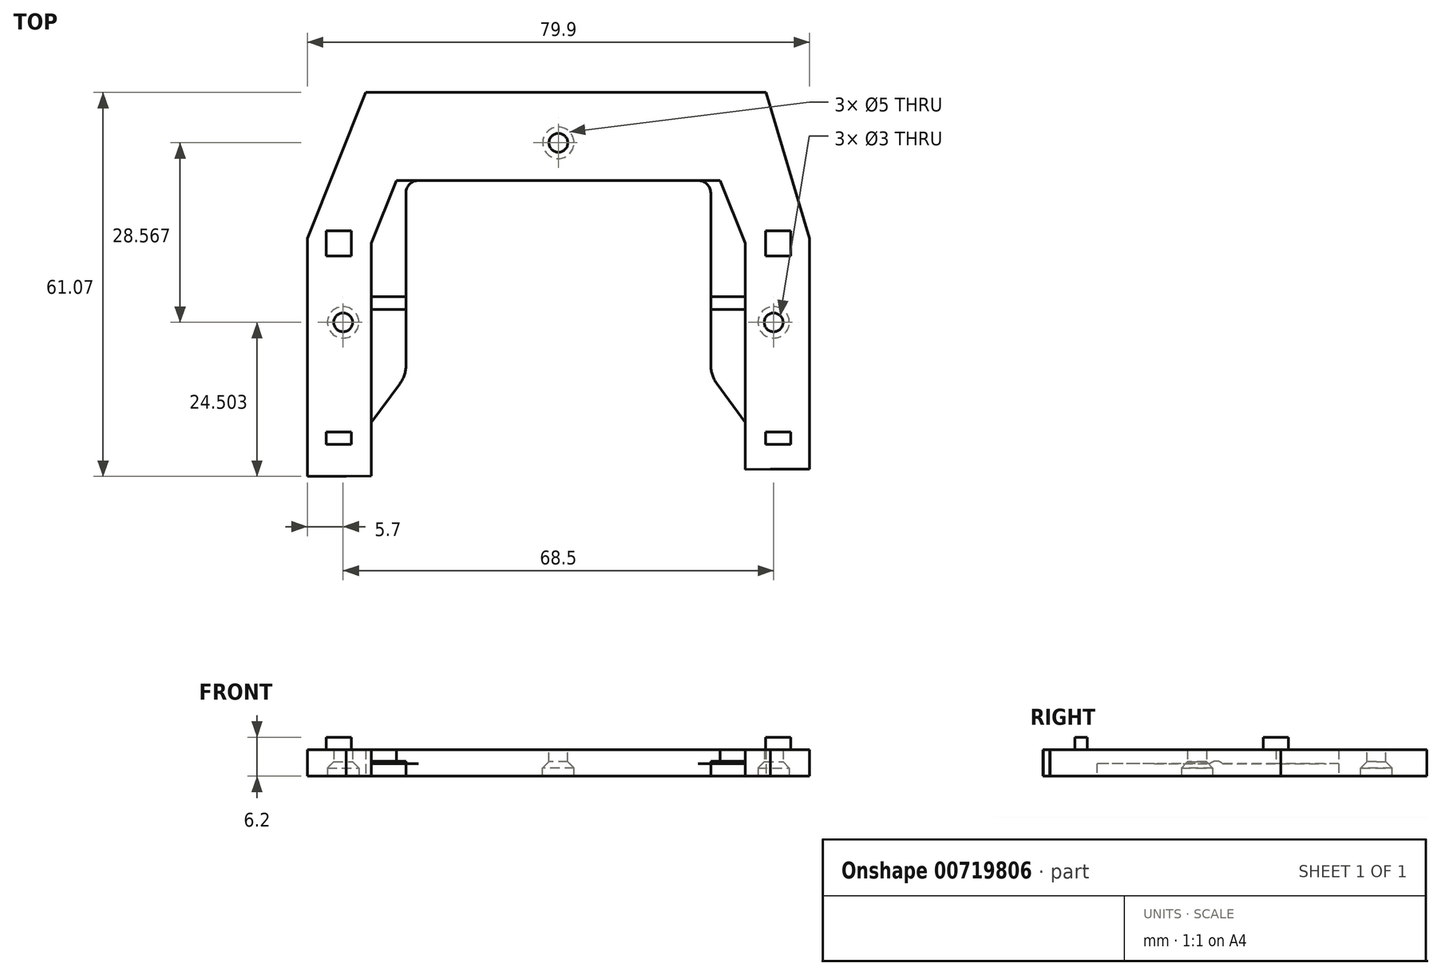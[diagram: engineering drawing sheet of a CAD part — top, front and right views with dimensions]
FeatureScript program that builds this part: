
annotation { "Feature Type Name" : "Feature", "Feature Type Description" : "" }
export const myFeature = defineFeature(function(context is Context, id is Id, definition is map)
    precondition{}
    {
        {
            var Q0;
            Q0=qCreatedBy(makeId("Top.planeOp"),FACE);
            var sketch = newSketch(context, id + "F0", { "sketchPlane" : qUnion([Q0])});
            skLineSegment(sketch, "E0.bottom", {"start": v(-25.5, 14.25) * mm, "end": v(26, 14.25) * mm});
            skLineSegment(sketch, "E0.left", {"start": v(-29.5, 4.25) * mm, "end": v(-29.5, -35.75) * mm});
            skLineSegment(sketch, "E0.right", {"start": v(30, 4.25) * mm, "end": v(30, -35.75) * mm});
            skLineSegment(sketch, "E1", {"start": v(-25.5, 14.25) * mm, "end": v(-29.5, 4.25) * mm});
            skPoint(sketch, "E2.orphan", {"position": v(-29.5, 14.25) * mm});
            skLineSegment(sketch, "E3", {"start": v(26, 14.25) * mm, "end": v(30, 4.25) * mm});
            skPoint(sketch, "E4.orphan", {"position": v(30, 14.25) * mm});
            skLineSegment(sketch, "E5.0", {"start": v(-24.2, 28.25) * mm, "end": v(-33.5, 5.02) * mm});
            skLineSegment(sketch, "E5.1", {"start": v(-33.5, -32.82) * mm, "end": v(34, -31.68) * mm});
            skLineSegment(sketch, "E5.2", {"start": v(34, 5.02) * mm, "end": v(34, -31.68) * mm});
            skLineSegment(sketch, "E5.3", {"start": v(-33.5, 5.02) * mm, "end": v(-33.5, -32.82) * mm});
            skLineSegment(sketch, "E5.4", {"start": v(27.1, 28.25) * mm, "end": v(34, 5.02) * mm});
            skLineSegment(sketch, "E5.5", {"start": v(-24.2, 28.25) * mm, "end": v(27.1, 28.25) * mm});
            skLineSegment(sketch, "E6", {"start": v(-29.5, -32.75) * mm, "end": v(-29.5, -35.75) * mm});
            skLineSegment(sketch, "E7", {"start": v(30, -32.75) * mm, "end": v(30, -35.75) * mm});
            skLineSegment(sketch, "E8.bottom", {"start": v(-29.5, -32.75) * mm, "end": v(30, -31.75) * mm});
            skLineSegment(sketch, "E8.left", {"start": v(-29.5, -32.75) * mm, "end": v(-29.5, -24.25) * mm});
            skLineSegment(sketch, "E8.right", {"start": v(30, -31.75) * mm, "end": v(30, -24.25) * mm});
            skLineSegment(sketch, "E9.top", {"start": v(-22, 14.25) * mm, "end": v(22.5, 14.25) * mm});
            skLineSegment(sketch, "E9.left", {"start": v(-24, -16.75) * mm, "end": v(-24, 12.25) * mm});
            skLineSegment(sketch, "E9.right", {"start": v(24.5, -16.75) * mm, "end": v(24.5, 12.25) * mm});
            skPoint(sketch, "E10.visualSharp", {"position": v(-24, 14.25) * mm});
            skArc(sketch, "E10.filletArc", {"start": v(-22, 14.25) * mm, "mid": v(-23.41, 13.66) * mm, "end": v(-24, 12.25) * mm});
            skPoint(sketch, "E11.visualSharp", {"position": v(24.5, 14.25) * mm});
            skArc(sketch, "E11.filletArc", {"start": v(24.5, 12.25) * mm, "mid": v(23.91, 13.66) * mm, "end": v(22.5, 14.25) * mm});
            skLineSegment(sketch, "E12", {"start": v(24.5, -16.75) * mm, "end": v(30, -24.25) * mm});
            skLineSegment(sketch, "E13", {"start": v(-24, -16.75) * mm, "end": v(-29.5, -24.25) * mm});
            skPoint(sketch, "E14.orphan", {"position": v(-29.5, -15.75) * mm});
            skPoint(sketch, "E15.orphan", {"position": v(30, -16.75) * mm});
            skSolve(sketch);
        }
        {
            var Q0;
            Q0=makeQuery(id+"F0.imprint","IMPRINT",FACE,{"disambiguationData":[TD([[makeQuery(id+"F0.imprint","IMPRINT",EDGE,{"derivedFrom":sQuery(id+"F0.wireOp",EDGE,"E0.bottom")}),-1.0]])]});
            extrude(context, id + "F1", {"entities" : qUnion([Q0]), "depth" : 2 * mm, "offsetDistance" : 25 * mm});
        }
        {
            var Q0;
            Q0=makeQuery(id+"F0.imprint","IMPRINT",FACE,{"disambiguationData":[TD([[makeQuery(id+"F0.imprint","IMPRINT",EDGE,{"derivedFrom":sQuery(id+"F0.wireOp",EDGE,"E0.bottom")}),1.0]])]});
            extrude(context, id + "F2", {"entities" : qUnion([Q0]), "operationType" : NewBodyOperationType.ADD, "depth" : 4.2 * mm, "offsetDistance" : 25 * mm});
        }
        {
            var Q0;
            Q0=makeQuery(id+"F2.opExtrude","SWEPT_FACE",FACE,{"disambiguationData":[OSD([sQuery(id+"F0.wireOp",EDGE,"E5.3")])]});
            var Q1;
            Q1=makeQuery(id+"F2.opExtrude","SWEPT_FACE",FACE,{"disambiguationData":[OSD([sQuery(id+"F0.wireOp",EDGE,"E5.0")])]});
            extrude(context, id + "F3", {"entities" : qUnion([Q0, Q1]), "operationType" : NewBodyOperationType.ADD, "depth" : 6.2 * mm, "offsetDistance" : 25 * mm});
        }
        {
            var Q0;
            Q0=makeQuery(id+"F2.opExtrude","SWEPT_FACE",FACE,{"disambiguationData":[OSD([sQuery(id+"F0.wireOp",EDGE,"E5.2")])]});
            var Q1;
            Q1=makeQuery(id+"F2.opExtrude","SWEPT_FACE",FACE,{"disambiguationData":[OSD([sQuery(id+"F0.wireOp",EDGE,"E5.4")])]});
            extrude(context, id + "F4", {"entities" : qUnion([Q0, Q1]), "operationType" : NewBodyOperationType.ADD, "depth" : 6.2 * mm, "offsetDistance" : 25 * mm});
        }
        {
            var Q0;
            {var subQ0=sQuery(id+"F0.wireOp",EDGE,"E5.4");var subQ1=sQuery(id+"F0.wireOp",EDGE,"E5.2");var subQ2=sQuery(id+"F0.wireOp",EDGE,"E5.3");var subQ3=sQuery(id+"F0.wireOp",EDGE,"E5.0");Q0=makeQuery(id+"F4.boolean.opBoolean","MERGE",FACE,{"derivedFrom":[makeQuery(id+"F3.boolean.opBoolean","MERGE",FACE,{"derivedFrom":[makeQuery(id+"F2.opExtrude","CAP_FACE",FACE,{"disambiguationData":[OSD([sQuery(id+"F0.wireOp",EDGE,"E0.bottom"),sQuery(id+"F0.wireOp",EDGE,"E0.left"),sQuery(id+"F0.wireOp",EDGE,"E0.right"),sQuery(id+"F0.wireOp",EDGE,"E1"),sQuery(id+"F0.wireOp",EDGE,"E3"),subQ3,sQuery(id+"F0.wireOp",EDGE,"E5.1"),subQ1,subQ2,subQ0,sQuery(id+"F0.wireOp",EDGE,"E5.5"),sQuery(id+"F0.wireOp",EDGE,"E8.left"),sQuery(id+"F0.wireOp",EDGE,"E8.right"),sQuery(id+"F0.wireOp",EDGE,"E9.top")])],"isStart":false}),makeQuery(id+"F3.opExtrude","SWEPT_FACE",FACE,{"disambiguationData":[OSD([subQ3]),TDD([makeQuery(id+"F2.opExtrude","CAP_EDGE",EDGE,{"disambiguationData":[OSD([subQ3])],"isStart":false})])]}),makeQuery(id+"F3.opExtrude","SWEPT_FACE",FACE,{"disambiguationData":[OSD([subQ2]),TDD([makeQuery(id+"F2.opExtrude","CAP_EDGE",EDGE,{"disambiguationData":[OSD([subQ2])],"isStart":false})])]})]}),makeQuery(id+"F4.opExtrude","SWEPT_FACE",FACE,{"disambiguationData":[OSD([subQ1]),TDD([makeQuery(id+"F2.opExtrude","CAP_EDGE",EDGE,{"disambiguationData":[OSD([subQ1])],"isStart":false})])]}),makeQuery(id+"F4.opExtrude","SWEPT_FACE",FACE,{"disambiguationData":[OSD([subQ0]),TDD([makeQuery(id+"F2.opExtrude","CAP_EDGE",EDGE,{"disambiguationData":[OSD([subQ0])],"isStart":false})])]})]});}
            var sketch = newSketch(context, id + "F5", { "sketchPlane" : qUnion([Q0])});
            skLineSegment(sketch, "E16.bottom", {"start": v(-36.7, -27.75) * mm, "end": v(-32.7, -27.75) * mm});
            skLineSegment(sketch, "E16.top", {"start": v(-36.7, -25.75) * mm, "end": v(-32.7, -25.75) * mm});
            skLineSegment(sketch, "E16.left", {"start": v(-36.7, -27.75) * mm, "end": v(-36.7, -25.75) * mm});
            skLineSegment(sketch, "E16.right", {"start": v(-32.7, -27.75) * mm, "end": v(-32.7, -25.75) * mm});
            skLineSegment(sketch, "E17.bottom", {"start": v(37.2, -27.75) * mm, "end": v(33.2, -27.75) * mm});
            skLineSegment(sketch, "E17.top", {"start": v(37.2, -25.75) * mm, "end": v(33.2, -25.75) * mm});
            skLineSegment(sketch, "E17.left", {"start": v(37.2, -27.75) * mm, "end": v(37.2, -25.75) * mm});
            skLineSegment(sketch, "E17.right", {"start": v(33.2, -27.75) * mm, "end": v(33.2, -25.75) * mm});
            skLineSegment(sketch, "E18.bottom", {"start": v(33.2, 2.25) * mm, "end": v(37.2, 2.25) * mm});
            skLineSegment(sketch, "E18.top", {"start": v(33.2, 6.25) * mm, "end": v(37.2, 6.25) * mm});
            skLineSegment(sketch, "E18.left", {"start": v(33.2, 2.25) * mm, "end": v(33.2, 6.25) * mm});
            skLineSegment(sketch, "E18.right", {"start": v(37.2, 2.25) * mm, "end": v(37.2, 6.25) * mm});
            skLineSegment(sketch, "E19.bottom", {"start": v(-36.7, 2.25) * mm, "end": v(-32.7, 2.25) * mm});
            skLineSegment(sketch, "E19.top", {"start": v(-36.7, 6.25) * mm, "end": v(-32.7, 6.25) * mm});
            skLineSegment(sketch, "E19.left", {"start": v(-36.7, 2.25) * mm, "end": v(-36.7, 6.25) * mm});
            skLineSegment(sketch, "E19.right", {"start": v(-32.7, 2.25) * mm, "end": v(-32.7, 6.25) * mm});
            skSolve(sketch);
        }
        {
            var Q0;
            Q0=qSketchRegion(id+"F5",true);
            extrude(context, id + "F6", {"entities" : qUnion([Q0]), "operationType" : NewBodyOperationType.ADD, "depth" : 2 * mm, "offsetDistance" : 25 * mm});
        }
        {
            var Q0;
            {var subQ0=sQuery(id+"F0.wireOp",EDGE,"E5.3");var subQ1=sQuery(id+"F0.wireOp",EDGE,"E5.0");var subQ2=sQuery(id+"F0.wireOp",EDGE,"E3");var subQ3=sQuery(id+"F0.wireOp",EDGE,"E1");var subQ4=sQuery(id+"F0.wireOp",EDGE,"E0.right");var subQ5=sQuery(id+"F0.wireOp",EDGE,"E0.left");var subQ6=sQuery(id+"F0.wireOp",EDGE,"E0.bottom");Q0=makeQuery(id+"F3.boolean.opBoolean","MERGE",FACE,{"derivedFrom":[makeQuery(id+"FPUi8WWa0XVN5Qz_1.opFillet","SPLIT",FACE,{"disambiguationData":[OD(0.0)],"derivedFrom":makeQuery(id+"F2.boolean.opBoolean","MERGE",FACE,{"derivedFrom":[makeQuery(id+"F1.opExtrude","CAP_FACE",FACE,{"disambiguationData":[OSD([subQ6,subQ5,subQ3,sQuery(id+"F0.wireOp",EDGE,"E9.left"),sQuery(id+"F0.wireOp",EDGE,"E10.filletArc"),sQuery(id+"F0.wireOp",EDGE,"E13")])],"isStart":true}),makeQuery(id+"F1.opExtrude","CAP_FACE",FACE,{"disambiguationData":[OSD([subQ6,subQ4,subQ2,sQuery(id+"F0.wireOp",EDGE,"E9.right"),sQuery(id+"F0.wireOp",EDGE,"E11.filletArc"),sQuery(id+"F0.wireOp",EDGE,"E12")])],"isStart":true}),makeQuery(id+"F2.opExtrude","CAP_FACE",FACE,{"disambiguationData":[OSD([subQ6,subQ5,subQ4,subQ3,subQ2,subQ1,sQuery(id+"F0.wireOp",EDGE,"E5.1"),sQuery(id+"F0.wireOp",EDGE,"E5.2"),subQ0,sQuery(id+"F0.wireOp",EDGE,"E5.4"),sQuery(id+"F0.wireOp",EDGE,"E5.5"),sQuery(id+"F0.wireOp",EDGE,"E8.left"),sQuery(id+"F0.wireOp",EDGE,"E8.right"),sQuery(id+"F0.wireOp",EDGE,"E9.top")])],"isStart":true})]})}),makeQuery(id+"F3.opExtrude","SWEPT_FACE",FACE,{"disambiguationData":[OSD([subQ1]),TDD([makeQuery(id+"F2.opExtrude","CAP_EDGE",EDGE,{"disambiguationData":[OSD([subQ1])],"isStart":true})])]}),makeQuery(id+"F3.opExtrude","SWEPT_FACE",FACE,{"disambiguationData":[OSD([subQ0]),TDD([makeQuery(id+"F2.opExtrude","CAP_EDGE",EDGE,{"disambiguationData":[OSD([subQ0])],"isStart":true})])]})]});}
            var sketch = newSketch(context, id + "F7", { "sketchPlane" : qUnion([Q0])});
            skCircle(sketch, "E20", {"center": v(-34, 8.32) * mm, "radius": 2.5 * mm});
            skCircle(sketch, "E21", {"center": v(34.5, 8.32) * mm, "radius": 2.5 * mm});
            skCircle(sketch, "E22", {"center": v(-34, 8.32) * mm, "radius": 1.5 * mm});
            skCircle(sketch, "E23", {"center": v(34.5, 8.32) * mm, "radius": 1.5 * mm});
            skSolve(sketch);
        }
        {
            var Q0;
            Q0=qSketchRegion(id+"F7",true);
            extrude(context, id + "F8", {"entities" : qUnion([Q0]), "operationType" : NewBodyOperationType.REMOVE, "oppositeDirection" : true, "depth" : 2.5 * mm, "offsetDistance" : 25 * mm});
        }
        {
            var Q0;
            {var subQ0=sQuery(id+"F0.wireOp",EDGE,"E5.3");var subQ1=sQuery(id+"F0.wireOp",EDGE,"E5.0");var subQ2=sQuery(id+"F0.wireOp",EDGE,"E3");var subQ3=sQuery(id+"F0.wireOp",EDGE,"E1");var subQ4=sQuery(id+"F0.wireOp",EDGE,"E0.right");var subQ5=sQuery(id+"F0.wireOp",EDGE,"E0.left");var subQ6=sQuery(id+"F0.wireOp",EDGE,"E0.bottom");Q0=makeQuery(id+"F8.boolean.opBoolean","SPLIT",FACE,{"disambiguationData":[TD([makeQuery(id+"F8.opExtrude","SWEPT_FACE",FACE,{"disambiguationData":[OSD([sQuery(id+"F7.wireOp",EDGE,"E22")])]})])],"derivedFrom":makeQuery(id+"F3.boolean.opBoolean","MERGE",FACE,{"derivedFrom":[makeQuery(id+"FPUi8WWa0XVN5Qz_1.opFillet","SPLIT",FACE,{"disambiguationData":[OD(0.0)],"derivedFrom":makeQuery(id+"F2.boolean.opBoolean","MERGE",FACE,{"derivedFrom":[makeQuery(id+"F1.opExtrude","CAP_FACE",FACE,{"disambiguationData":[OSD([subQ6,subQ5,subQ3,sQuery(id+"F0.wireOp",EDGE,"E9.left"),sQuery(id+"F0.wireOp",EDGE,"E10.filletArc"),sQuery(id+"F0.wireOp",EDGE,"E13")])],"isStart":true}),makeQuery(id+"F1.opExtrude","CAP_FACE",FACE,{"disambiguationData":[OSD([subQ6,subQ4,subQ2,sQuery(id+"F0.wireOp",EDGE,"E9.right"),sQuery(id+"F0.wireOp",EDGE,"E11.filletArc"),sQuery(id+"F0.wireOp",EDGE,"E12")])],"isStart":true}),makeQuery(id+"F2.opExtrude","CAP_FACE",FACE,{"disambiguationData":[OSD([subQ6,subQ5,subQ4,subQ3,subQ2,subQ1,sQuery(id+"F0.wireOp",EDGE,"E5.1"),sQuery(id+"F0.wireOp",EDGE,"E5.2"),subQ0,sQuery(id+"F0.wireOp",EDGE,"E5.4"),sQuery(id+"F0.wireOp",EDGE,"E5.5"),sQuery(id+"F0.wireOp",EDGE,"E8.left"),sQuery(id+"F0.wireOp",EDGE,"E8.right"),sQuery(id+"F0.wireOp",EDGE,"E9.top")])],"isStart":true})]})}),makeQuery(id+"F3.opExtrude","SWEPT_FACE",FACE,{"disambiguationData":[OSD([subQ1]),TDD([makeQuery(id+"F2.opExtrude","CAP_EDGE",EDGE,{"disambiguationData":[OSD([subQ1])],"isStart":true})])]}),makeQuery(id+"F3.opExtrude","SWEPT_FACE",FACE,{"disambiguationData":[OSD([subQ0]),TDD([makeQuery(id+"F2.opExtrude","CAP_EDGE",EDGE,{"disambiguationData":[OSD([subQ0])],"isStart":true})])]})]})});}
            var Q1;
            {var subQ0=sQuery(id+"F0.wireOp",EDGE,"E5.2");var subQ1=sQuery(id+"F0.wireOp",EDGE,"E5.4");var subQ2=sQuery(id+"F0.wireOp",EDGE,"E3");var subQ3=sQuery(id+"F0.wireOp",EDGE,"E1");var subQ4=sQuery(id+"F0.wireOp",EDGE,"E0.right");var subQ5=sQuery(id+"F0.wireOp",EDGE,"E0.left");var subQ6=sQuery(id+"F0.wireOp",EDGE,"E0.bottom");Q1=makeQuery(id+"F8.boolean.opBoolean","SPLIT",FACE,{"disambiguationData":[TD([makeQuery(id+"F8.opExtrude","SWEPT_FACE",FACE,{"disambiguationData":[OSD([sQuery(id+"F7.wireOp",EDGE,"E23")])]})])],"derivedFrom":makeQuery(id+"F4.boolean.opBoolean","MERGE",FACE,{"derivedFrom":[makeQuery(id+"FPUi8WWa0XVN5Qz_1.opFillet","SPLIT",FACE,{"disambiguationData":[OD(1.0)],"derivedFrom":makeQuery(id+"F2.boolean.opBoolean","MERGE",FACE,{"derivedFrom":[makeQuery(id+"F1.opExtrude","CAP_FACE",FACE,{"disambiguationData":[OSD([subQ6,subQ5,subQ3,sQuery(id+"F0.wireOp",EDGE,"E9.left"),sQuery(id+"F0.wireOp",EDGE,"E10.filletArc"),sQuery(id+"F0.wireOp",EDGE,"E13")])],"isStart":true}),makeQuery(id+"F1.opExtrude","CAP_FACE",FACE,{"disambiguationData":[OSD([subQ6,subQ4,subQ2,sQuery(id+"F0.wireOp",EDGE,"E9.right"),sQuery(id+"F0.wireOp",EDGE,"E11.filletArc"),sQuery(id+"F0.wireOp",EDGE,"E12")])],"isStart":true}),makeQuery(id+"F2.opExtrude","CAP_FACE",FACE,{"disambiguationData":[OSD([subQ6,subQ5,subQ4,subQ3,subQ2,sQuery(id+"F0.wireOp",EDGE,"E5.0"),sQuery(id+"F0.wireOp",EDGE,"E5.1"),subQ0,sQuery(id+"F0.wireOp",EDGE,"E5.3"),subQ1,sQuery(id+"F0.wireOp",EDGE,"E5.5"),sQuery(id+"F0.wireOp",EDGE,"E8.left"),sQuery(id+"F0.wireOp",EDGE,"E8.right"),sQuery(id+"F0.wireOp",EDGE,"E9.top")])],"isStart":true})]})}),makeQuery(id+"F4.opExtrude","SWEPT_FACE",FACE,{"disambiguationData":[OSD([subQ1]),TDD([makeQuery(id+"F2.opExtrude","CAP_EDGE",EDGE,{"disambiguationData":[OSD([subQ1])],"isStart":true})])]}),makeQuery(id+"F4.opExtrude","SWEPT_FACE",FACE,{"disambiguationData":[OSD([subQ0]),TDD([makeQuery(id+"F2.opExtrude","CAP_EDGE",EDGE,{"disambiguationData":[OSD([subQ0])],"isStart":true})])]})]})});}
            extrude(context, id + "F9", {"entities" : qUnion([Q0, Q1]), "operationType" : NewBodyOperationType.REMOVE, "oppositeDirection" : true, "depth" : 4.5 * mm, "offsetDistance" : 25 * mm});
        }
        {
            var Q0;
            Q0=makeQuery(id+"F1.opExtrude","SWEPT_EDGE",EDGE,{"disambiguationData":[OSD([sQuery(id+"F0.wireOp",EDGE,"E9.right"),sQuery(id+"F0.wireOp",EDGE,"E12")])]});
            var Q1;
            Q1=makeQuery(id+"F1.opExtrude","SWEPT_EDGE",EDGE,{"disambiguationData":[OSD([sQuery(id+"F0.wireOp",EDGE,"E9.left"),sQuery(id+"F0.wireOp",EDGE,"E13")])]});
            fillet(context, id + "F10", {"entities" : qUnion([Q0, Q1]), "radius" : 5 * mm, "tangentPropagation" : true, "allowEdgeOverflow" : false});
        }
        {
            var Q0;
            {var subQ0=sQuery(id+"F0.wireOp",EDGE,"E5.4");var subQ1=sQuery(id+"F0.wireOp",EDGE,"E5.2");var subQ2=sQuery(id+"F0.wireOp",EDGE,"E5.3");var subQ3=sQuery(id+"F0.wireOp",EDGE,"E5.0");Q0=makeQuery(id+"F4.boolean.opBoolean","MERGE",FACE,{"derivedFrom":[makeQuery(id+"F3.boolean.opBoolean","MERGE",FACE,{"derivedFrom":[makeQuery(id+"F2.opExtrude","CAP_FACE",FACE,{"disambiguationData":[OSD([sQuery(id+"F0.wireOp",EDGE,"E0.bottom"),sQuery(id+"F0.wireOp",EDGE,"E0.left"),sQuery(id+"F0.wireOp",EDGE,"E0.right"),sQuery(id+"F0.wireOp",EDGE,"E1"),sQuery(id+"F0.wireOp",EDGE,"E3"),subQ3,sQuery(id+"F0.wireOp",EDGE,"E5.1"),subQ1,subQ2,subQ0,sQuery(id+"F0.wireOp",EDGE,"E5.5"),sQuery(id+"F0.wireOp",EDGE,"E8.left"),sQuery(id+"F0.wireOp",EDGE,"E8.right"),sQuery(id+"F0.wireOp",EDGE,"E9.top")])],"isStart":false}),makeQuery(id+"F3.opExtrude","SWEPT_FACE",FACE,{"disambiguationData":[OSD([subQ3]),TDD([makeQuery(id+"F2.opExtrude","CAP_EDGE",EDGE,{"disambiguationData":[OSD([subQ3])],"isStart":false})])]}),makeQuery(id+"F3.opExtrude","SWEPT_FACE",FACE,{"disambiguationData":[OSD([subQ2]),TDD([makeQuery(id+"F2.opExtrude","CAP_EDGE",EDGE,{"disambiguationData":[OSD([subQ2])],"isStart":false})])]})]}),makeQuery(id+"F4.opExtrude","SWEPT_FACE",FACE,{"disambiguationData":[OSD([subQ1]),TDD([makeQuery(id+"F2.opExtrude","CAP_EDGE",EDGE,{"disambiguationData":[OSD([subQ1])],"isStart":false})])]}),makeQuery(id+"F4.opExtrude","SWEPT_FACE",FACE,{"disambiguationData":[OSD([subQ0]),TDD([makeQuery(id+"F2.opExtrude","CAP_EDGE",EDGE,{"disambiguationData":[OSD([subQ0])],"isStart":false})])]})]});}
            var sketch = newSketch(context, id + "F11", { "sketchPlane" : qUnion([Q0])});
            skCircle(sketch, "E24", {"center": v(0.25, 20.25) * mm, "radius": 1.5 * mm});
            skCircle(sketch, "E25", {"center": v(0.25, 20.25) * mm, "radius": 2.5 * mm});
            skSolve(sketch);
        }
        {
            var Q0;
            Q0=qSketchRegion(id+"F11",true);
            extrude(context, id + "F12", {"entities" : qUnion([Q0]), "operationType" : NewBodyOperationType.REMOVE, "oppositeDirection" : true, "depth" : 6.8 * mm, "offsetDistance" : 25 * mm, "hasSecondDirection" : true, "secondDirectionOppositeDirection" : true, "secondDirectionDepth" : 1.7 * mm});
        }
        {
            var Q0;
            Q0=makeQuery(id+"F11.imprint","IMPRINT",FACE,{"disambiguationData":[TD([[makeQuery(id+"F11.imprint","IMPRINT",EDGE,{"derivedFrom":sQuery(id+"F11.wireOp",EDGE,"E24")}),1.0]])]});
            extrude(context, id + "F13", {"entities" : qUnion([Q0]), "operationType" : NewBodyOperationType.REMOVE, "oppositeDirection" : true, "depth" : 4.2 * mm, "offsetDistance" : 25 * mm});
        }
        {
            var Q0;
            Q0=makeQuery(id+"F1.opExtrude","CAP_FACE",FACE,{"disambiguationData":[OSD([sQuery(id+"F0.wireOp",EDGE,"E0.bottom"),sQuery(id+"F0.wireOp",EDGE,"E0.right"),sQuery(id+"F0.wireOp",EDGE,"E3"),sQuery(id+"F0.wireOp",EDGE,"E9.right"),sQuery(id+"F0.wireOp",EDGE,"E11.filletArc"),sQuery(id+"F0.wireOp",EDGE,"E12")])],"isStart":false});
            var sketch = newSketch(context, id + "F14", { "sketchPlane" : qUnion([Q0])});
            skLineSegment(sketch, "E26.bottom", {"start": v(30, -6.25) * mm, "end": v(24.5, -6.25) * mm});
            skLineSegment(sketch, "E26.top", {"start": v(30, -4.25) * mm, "end": v(24.5, -4.25) * mm});
            skLineSegment(sketch, "E26.left", {"start": v(30, -6.25) * mm, "end": v(30, -4.25) * mm});
            skLineSegment(sketch, "E26.right", {"start": v(24.5, -6.25) * mm, "end": v(24.5, -4.25) * mm});
            skLineSegment(sketch, "E27.bottom", {"start": v(-29.5, -4.25) * mm, "end": v(-24, -4.25) * mm});
            skLineSegment(sketch, "E27.top", {"start": v(-29.5, -6.25) * mm, "end": v(-24, -6.25) * mm});
            skLineSegment(sketch, "E27.left", {"start": v(-29.5, -4.25) * mm, "end": v(-29.5, -6.25) * mm});
            skLineSegment(sketch, "E27.right", {"start": v(-24, -4.25) * mm, "end": v(-24, -6.25) * mm});
            skSolve(sketch);
        }
        {
            var Q0;
            Q0 = qSketchRegion(id + "F14", true);
            extrude(context, id + "F15", {"entities" : qUnion([Q0]), "operationType" : NewBodyOperationType.ADD, "depth" : 0.4 * mm, "offsetDistance" : 25 * mm});
        }
        {
            var Q0;
            Q0=makeQuery(id+"F15.opExtrude","CAP_EDGE",EDGE,{"disambiguationData":[OSD([sQuery(id+"F14.wireOp",EDGE,"E27.top")])],"isStart":false});
            var Q1;
            Q1=makeQuery(id+"F15.opExtrude","CAP_EDGE",EDGE,{"disambiguationData":[OSD([sQuery(id+"F14.wireOp",EDGE,"E27.bottom")])],"isStart":false});
            var Q2;
            Q2=makeQuery(id+"F15.opExtrude","CAP_EDGE",EDGE,{"disambiguationData":[OSD([sQuery(id+"F14.wireOp",EDGE,"E26.top")])],"isStart":false});
            var Q3;
            Q3=makeQuery(id+"F15.opExtrude","CAP_EDGE",EDGE,{"disambiguationData":[OSD([sQuery(id+"F14.wireOp",EDGE,"E26.bottom")])],"isStart":false});
            fillet(context, id + "F16", {"entities" : qUnion([Q0, Q1, Q2, Q3]), "radius" : 1.4 * mm, "tangentPropagation" : true, "allowEdgeOverflow" : false});
        }
        {
            var Q0;
            Q0=makeQuery(id+"F8.boolean.opBoolean","COPY",EDGE,{"derivedFrom":makeQuery(id+"F8.opExtrude","CAP_EDGE",EDGE,{"disambiguationData":[OSD([sQuery(id+"F7.wireOp",EDGE,"E20")])],"isStart":false})});
            var Q1;
            Q1=makeQuery(id+"F8.boolean.opBoolean","COPY",EDGE,{"derivedFrom":makeQuery(id+"F8.opExtrude","CAP_EDGE",EDGE,{"disambiguationData":[OSD([sQuery(id+"F7.wireOp",EDGE,"E21")])],"isStart":false})});
            var Q2;
            Q2=makeQuery(id+"F12.boolean.opBoolean","COPY",EDGE,{"derivedFrom":makeQuery(id+"F12.opExtrude","CAP_EDGE",EDGE,{"disambiguationData":[OSD([sQuery(id+"F11.wireOp",EDGE,"E25")])],"isStart":true})});
            chamfer(context, id + "F17", {"entities" : qUnion([Q0, Q1, Q2]), "width" : 1.2 * mm, "tangentPropagation" : true});
        }
    });
